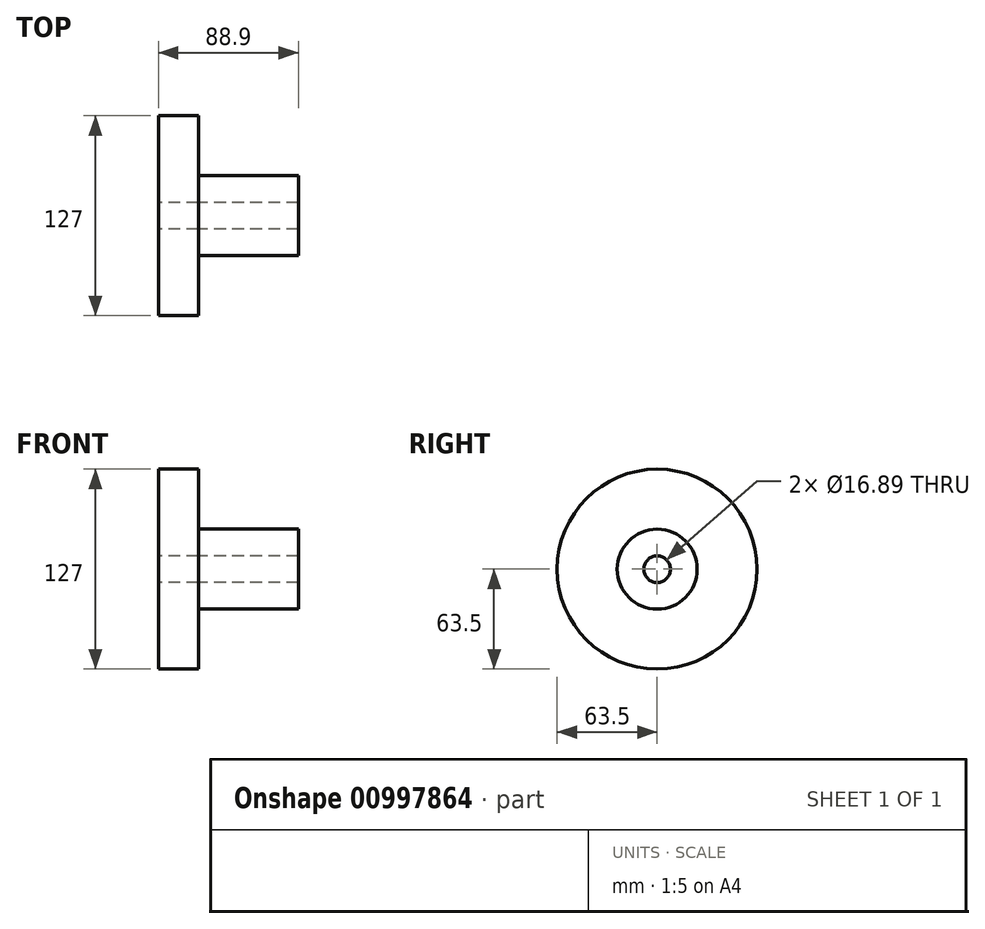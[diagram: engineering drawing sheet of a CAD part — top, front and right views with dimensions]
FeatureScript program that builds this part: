
annotation { "Feature Type Name" : "Feature", "Feature Type Description" : "" }
export const myFeature = defineFeature(function(context is Context, id is Id, definition is map)
    precondition{}
    {
        {
            var Q0;
            Q0=qCreatedBy(makeId("Front.planeOp"),FACE);
            var sketch = newSketch(context, id + "F0", { "sketchPlane" : qUnion([Q0])});
            skLineSegment(sketch, "E0.bottom", {"start": v(0, 0) * mm, "end": v(63.5, 0) * mm});
            skLineSegment(sketch, "E0.top", {"start": v(0, 25.4) * mm, "end": v(63.5, 25.4) * mm});
            skLineSegment(sketch, "E0.left", {"start": v(0, 0) * mm, "end": v(0, 25.4) * mm});
            skLineSegment(sketch, "E0.right", {"start": v(63.5, 0) * mm, "end": v(63.5, 25.4) * mm});
            skSolve(sketch);
        }
        {
            var Q0;
            Q0=qCreatedBy(makeId("Front.planeOp"),FACE);
            var sketch = newSketch(context, id + "F1", { "sketchPlane" : qUnion([Q0])});
            skLineSegment(sketch, "E1.bottom", {"start": v(0, 0) * mm, "end": v(-25.4, 0) * mm});
            skLineSegment(sketch, "E1.top", {"start": v(0, 63.5) * mm, "end": v(-25.4, 63.5) * mm});
            skLineSegment(sketch, "E1.left", {"start": v(0, 0) * mm, "end": v(0, 63.5) * mm});
            skLineSegment(sketch, "E1.right", {"start": v(-25.4, 0) * mm, "end": v(-25.4, 63.5) * mm});
            skSolve(sketch);
        }
        {
            var Q0;
            Q0=qCreatedBy(makeId("Front.planeOp"),FACE);
            var sketch = newSketch(context, id + "F2", { "sketchPlane" : qUnion([Q0])});
            skLineSegment(sketch, "E2", {"start": v(-56.97, 0) * mm, "end": v(75.44, 0) * mm, "construction": true});
            skSolve(sketch);
        }
        {
            var Q0;
            Q0=makeQuery(id+"F1.imprint","IMPRINT",FACE,{"disambiguationData":[TD([[makeQuery(id+"F1.imprint","IMPRINT",EDGE,{"derivedFrom":sQuery(id+"F1.wireOp",EDGE,"E1.bottom")}),-1.0]])]});
            var Q1;
            Q1=makeQuery(id+"F0.imprint","IMPRINT",FACE,{"disambiguationData":[TD([[makeQuery(id+"F0.imprint","IMPRINT",EDGE,{"derivedFrom":sQuery(id+"F0.wireOp",EDGE,"E0.bottom")}),1.0]])]});
            var Q2;
            Q2=sQuery(id+"F2.wireOp",EDGE,"E2");
            revolve(context, id + "F3", {"surfaceOperationType" : NewSurfaceOperationType.NEW, "entities" : qUnion([Q0, Q1]), "axis" : qUnion([Q2]), "revolveType" : RevolveType.FULL});
        }
        {
            var Q0;
            Q0=makeQuery(id+"F3.opRevolve","SWEPT_FACE",FACE,{"disambiguationData":[OSD([sQuery(id+"F1.wireOp",EDGE,"E1.right")])]});
            var sketch = newSketch(context, id + "F4", { "sketchPlane" : qUnion([Q0])});
            skCircle(sketch, "E3", {"center": v(0, 0) * mm, "radius": 8.45 * mm});
            skSolve(sketch);
        }
        {
            var Q0;
            Q0=makeQuery(id+"F4.imprint","IMPRINT",FACE,{"disambiguationData":[TD([[makeQuery(id+"F4.imprint","IMPRINT",EDGE,{"derivedFrom":sQuery(id+"F4.wireOp",EDGE,"E3")}),1.0]])]});
            var Q1;
            Q1=makeQuery(id+"F3.opRevolve","SWEPT_FACE",FACE,{"disambiguationData":[OSD([sQuery(id+"F0.wireOp",EDGE,"E0.right")])]});
            extrude(context, id + "F5", {"entities" : qUnion([Q0]), "operationType" : NewBodyOperationType.REMOVE, "endBound" : BoundingType.UP_TO_SURFACE, "oppositeDirection" : true, "depth" : 25.4 * mm, "endBoundEntityFace" : qUnion([Q1]), "offsetDistance" : 25.4 * mm});
        }
    });
